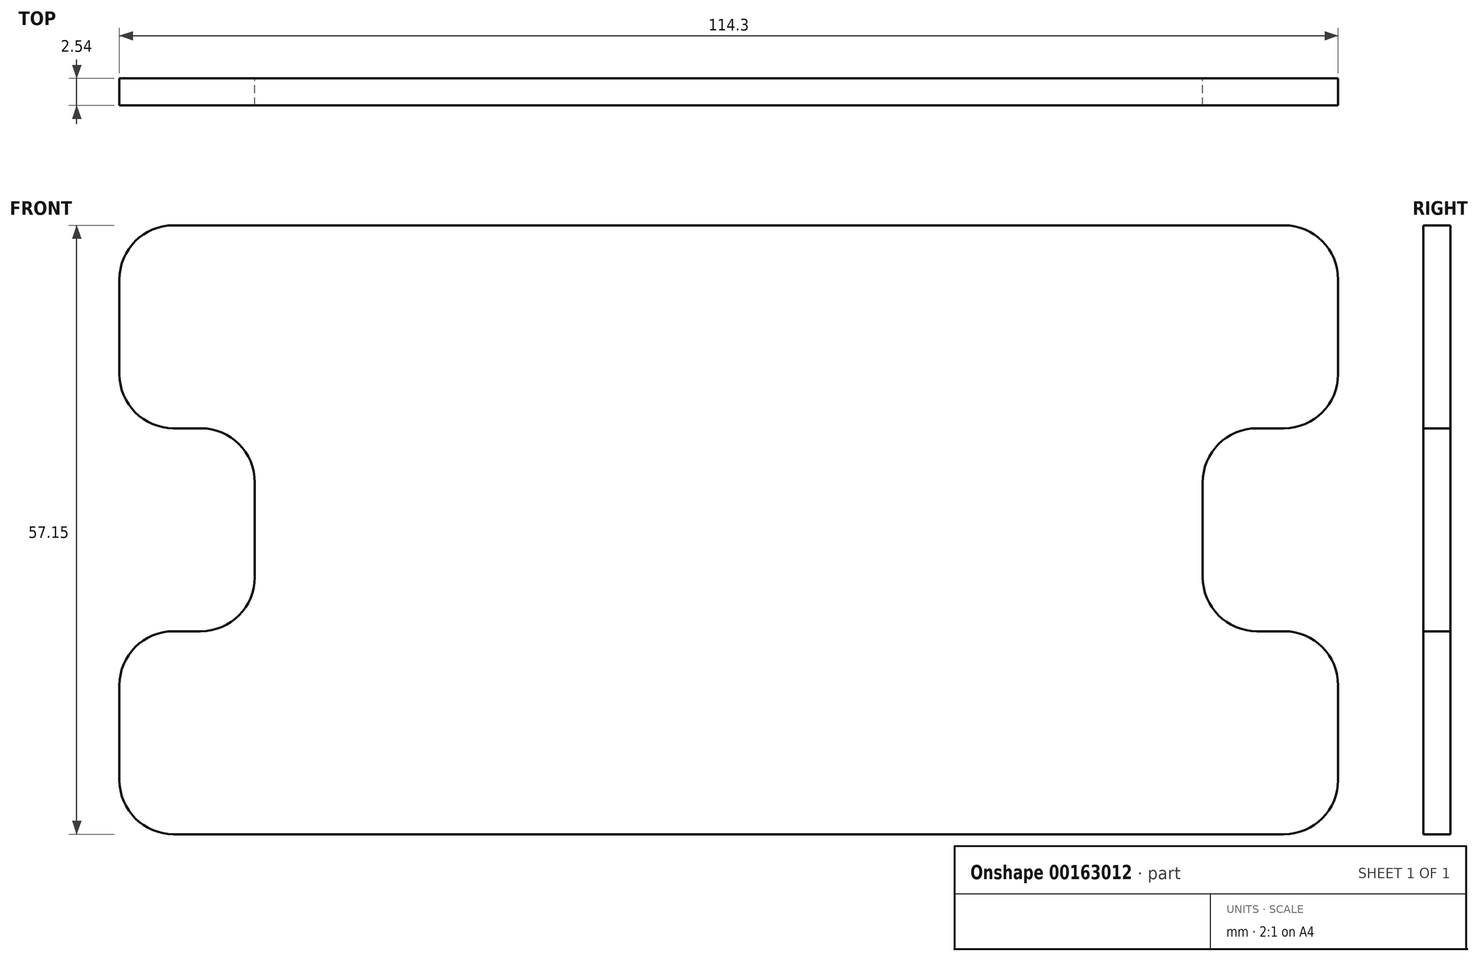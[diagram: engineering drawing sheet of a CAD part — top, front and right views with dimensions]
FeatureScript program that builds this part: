
annotation { "Feature Type Name" : "Feature", "Feature Type Description" : "" }
export const myFeature = defineFeature(function(context is Context, id is Id, definition is map)
    precondition{}
    {
        {
            var Q0;
            Q0=qCreatedBy(makeId("Front.planeOp"),FACE);
            var sketch = newSketch(context, id + "F0", { "sketchPlane" : qUnion([Q0])});
            skLineSegment(sketch, "E0", {"start": v(61.66, 55.06) * mm, "end": v(-52.64, 55.06) * mm});
            skLineSegment(sketch, "E1", {"start": v(61.66, 55.06) * mm, "end": v(61.66, 36.01) * mm});
            skLineSegment(sketch, "E2", {"start": v(61.66, 36.01) * mm, "end": v(48.96, 36.01) * mm});
            skLineSegment(sketch, "E3", {"start": v(48.96, 36.01) * mm, "end": v(48.96, 16.96) * mm});
            skLineSegment(sketch, "E4", {"start": v(48.96, 16.96) * mm, "end": v(61.66, 16.96) * mm});
            skLineSegment(sketch, "E5", {"start": v(61.66, 16.96) * mm, "end": v(61.66, -2.09) * mm});
            skLineSegment(sketch, "E6", {"start": v(61.66, -2.09) * mm, "end": v(-52.64, -2.09) * mm});
            skLineSegment(sketch, "E7", {"start": v(-52.64, -2.09) * mm, "end": v(-52.64, 16.96) * mm});
            skLineSegment(sketch, "E8", {"start": v(-52.64, 16.96) * mm, "end": v(-39.94, 16.96) * mm});
            skLineSegment(sketch, "E9", {"start": v(-39.94, 16.96) * mm, "end": v(-39.94, 36.01) * mm});
            skLineSegment(sketch, "E10", {"start": v(-39.94, 36.01) * mm, "end": v(-52.64, 36.01) * mm});
            skLineSegment(sketch, "E11", {"start": v(-52.64, 55.06) * mm, "end": v(-52.64, 36.01) * mm});
            skSolve(sketch);
        }
        {
            var Q0;
            Q0 = qSketchRegion(id + "F0", true);
            extrude(context, id + "F1", {"entities" : qUnion([Q0]), "depth" : 2.54 * mm});
        }
        {
            var Q0;
            Q0=makeQuery(id+"F1.opExtrude","SWEPT_EDGE",EDGE,{"disambiguationData":[OSD([sQuery(id+"F0.wireOp",EDGE,"E0"),sQuery(id+"F0.wireOp",EDGE,"E1")])]});
            var Q1;
            Q1=makeQuery(id+"F1.opExtrude","SWEPT_EDGE",EDGE,{"disambiguationData":[OSD([sQuery(id+"F0.wireOp",EDGE,"E1"),sQuery(id+"F0.wireOp",EDGE,"E2")])]});
            var Q2;
            Q2=makeQuery(id+"F1.opExtrude","SWEPT_EDGE",EDGE,{"disambiguationData":[OSD([sQuery(id+"F0.wireOp",EDGE,"E2"),sQuery(id+"F0.wireOp",EDGE,"E3")])]});
            var Q3;
            Q3=makeQuery(id+"F1.opExtrude","SWEPT_EDGE",EDGE,{"disambiguationData":[OSD([sQuery(id+"F0.wireOp",EDGE,"E3"),sQuery(id+"F0.wireOp",EDGE,"E4")])]});
            var Q4;
            Q4=makeQuery(id+"F1.opExtrude","SWEPT_EDGE",EDGE,{"disambiguationData":[OSD([sQuery(id+"F0.wireOp",EDGE,"E4"),sQuery(id+"F0.wireOp",EDGE,"E5")])]});
            var Q5;
            Q5=makeQuery(id+"F1.opExtrude","SWEPT_EDGE",EDGE,{"disambiguationData":[OSD([sQuery(id+"F0.wireOp",EDGE,"E5"),sQuery(id+"F0.wireOp",EDGE,"E6")])]});
            var Q6;
            Q6=makeQuery(id+"F1.opExtrude","SWEPT_EDGE",EDGE,{"disambiguationData":[OSD([sQuery(id+"F0.wireOp",EDGE,"E8"),sQuery(id+"F0.wireOp",EDGE,"E9")])]});
            var Q7;
            Q7=makeQuery(id+"F1.opExtrude","SWEPT_EDGE",EDGE,{"disambiguationData":[OSD([sQuery(id+"F0.wireOp",EDGE,"E9"),sQuery(id+"F0.wireOp",EDGE,"E10")])]});
            var Q8;
            Q8=makeQuery(id+"F1.opExtrude","SWEPT_EDGE",EDGE,{"disambiguationData":[OSD([sQuery(id+"F0.wireOp",EDGE,"E10"),sQuery(id+"F0.wireOp",EDGE,"E11")])]});
            var Q9;
            Q9=makeQuery(id+"F1.opExtrude","SWEPT_EDGE",EDGE,{"disambiguationData":[OSD([sQuery(id+"F0.wireOp",EDGE,"E0"),sQuery(id+"F0.wireOp",EDGE,"E11")])]});
            var Q10;
            Q10=makeQuery(id+"F1.opExtrude","SWEPT_EDGE",EDGE,{"disambiguationData":[OSD([sQuery(id+"F0.wireOp",EDGE,"E7"),sQuery(id+"F0.wireOp",EDGE,"E8")])]});
            var Q11;
            Q11=makeQuery(id+"F1.opExtrude","SWEPT_EDGE",EDGE,{"disambiguationData":[OSD([sQuery(id+"F0.wireOp",EDGE,"E6"),sQuery(id+"F0.wireOp",EDGE,"E7")])]});
            fillet(context, id + "F2", {"entities" : qUnion([Q0, Q1, Q2, Q3, Q4, Q5, Q6, Q7, Q8, Q9, Q10, Q11]), "radius" : 5.08 * mm, "tangentPropagation" : true, "allowEdgeOverflow" : false});
        }
    });
